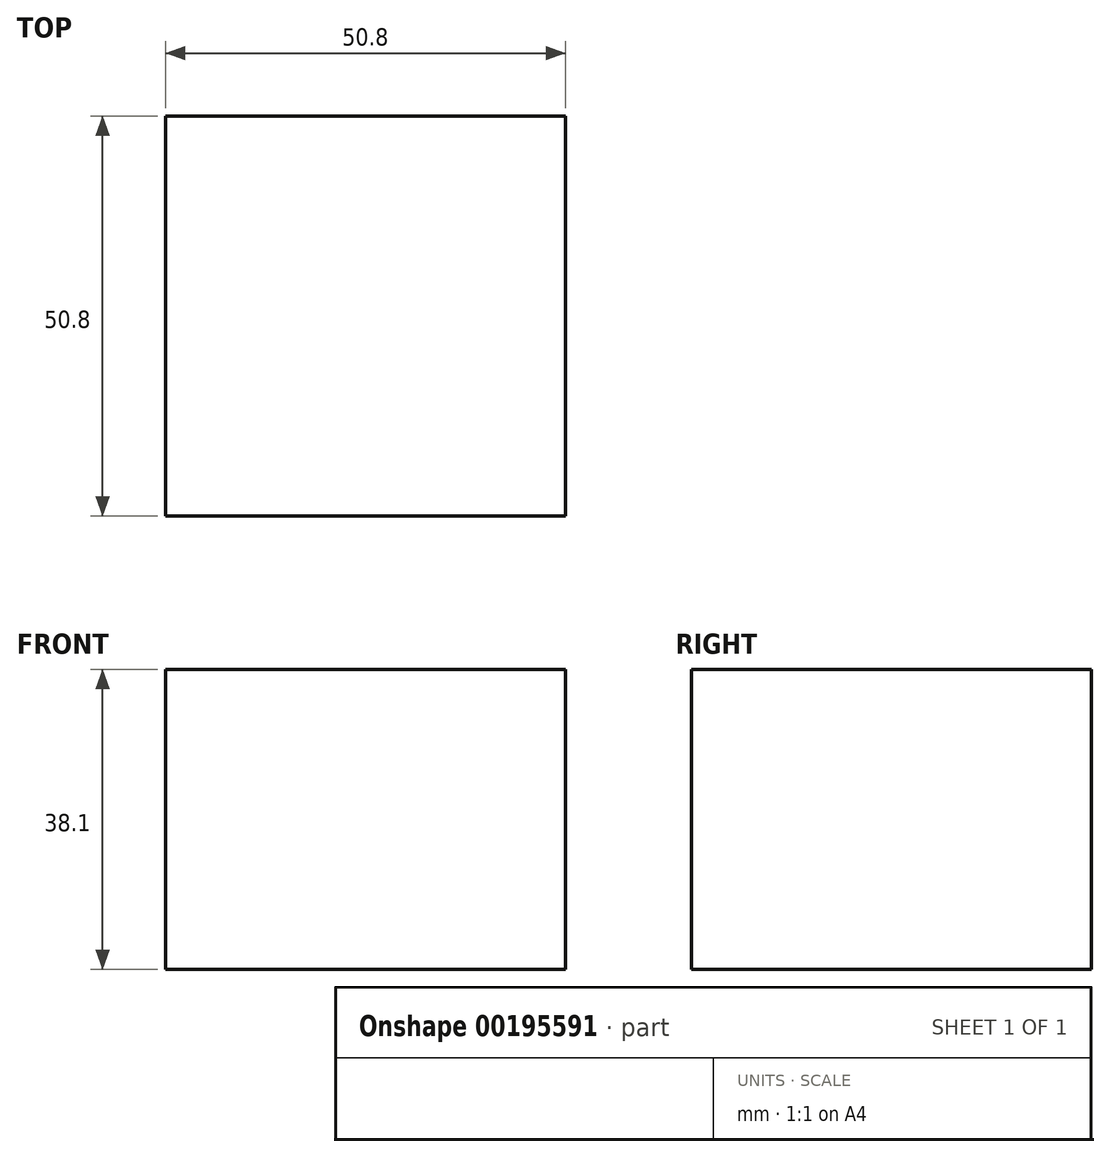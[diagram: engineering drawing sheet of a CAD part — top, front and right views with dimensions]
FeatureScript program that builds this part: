
annotation { "Feature Type Name" : "Feature", "Feature Type Description" : "" }
export const myFeature = defineFeature(function(context is Context, id is Id, definition is map)
    precondition{}
    {
        {
            var Q0;
            Q0=qCreatedBy(makeId("Top.planeOp"),FACE);
            var sketch = newSketch(context, id + "F0", { "sketchPlane" : qUnion([Q0])});
            skLineSegment(sketch, "E0.bottom", {"start": v(25.4, 25.4) * mm, "end": v(-25.4, 25.4) * mm});
            skLineSegment(sketch, "E0.top", {"start": v(25.4, -25.4) * mm, "end": v(-25.4, -25.4) * mm});
            skLineSegment(sketch, "E0.left", {"start": v(25.4, 25.4) * mm, "end": v(25.4, -25.4) * mm});
            skLineSegment(sketch, "E0.right", {"start": v(-25.4, 25.4) * mm, "end": v(-25.4, -25.4) * mm});
            skPoint(sketch, "E0.middle", {"position": v(0, 0) * mm});
            skSolve(sketch);
        }
        {
            var Q0;
            Q0 = qSketchRegion(id + "F0", true);
            extrude(context, id + "F1", {"entities" : qUnion([Q0]), "depth" : 38.1 * mm});
        }
    });
